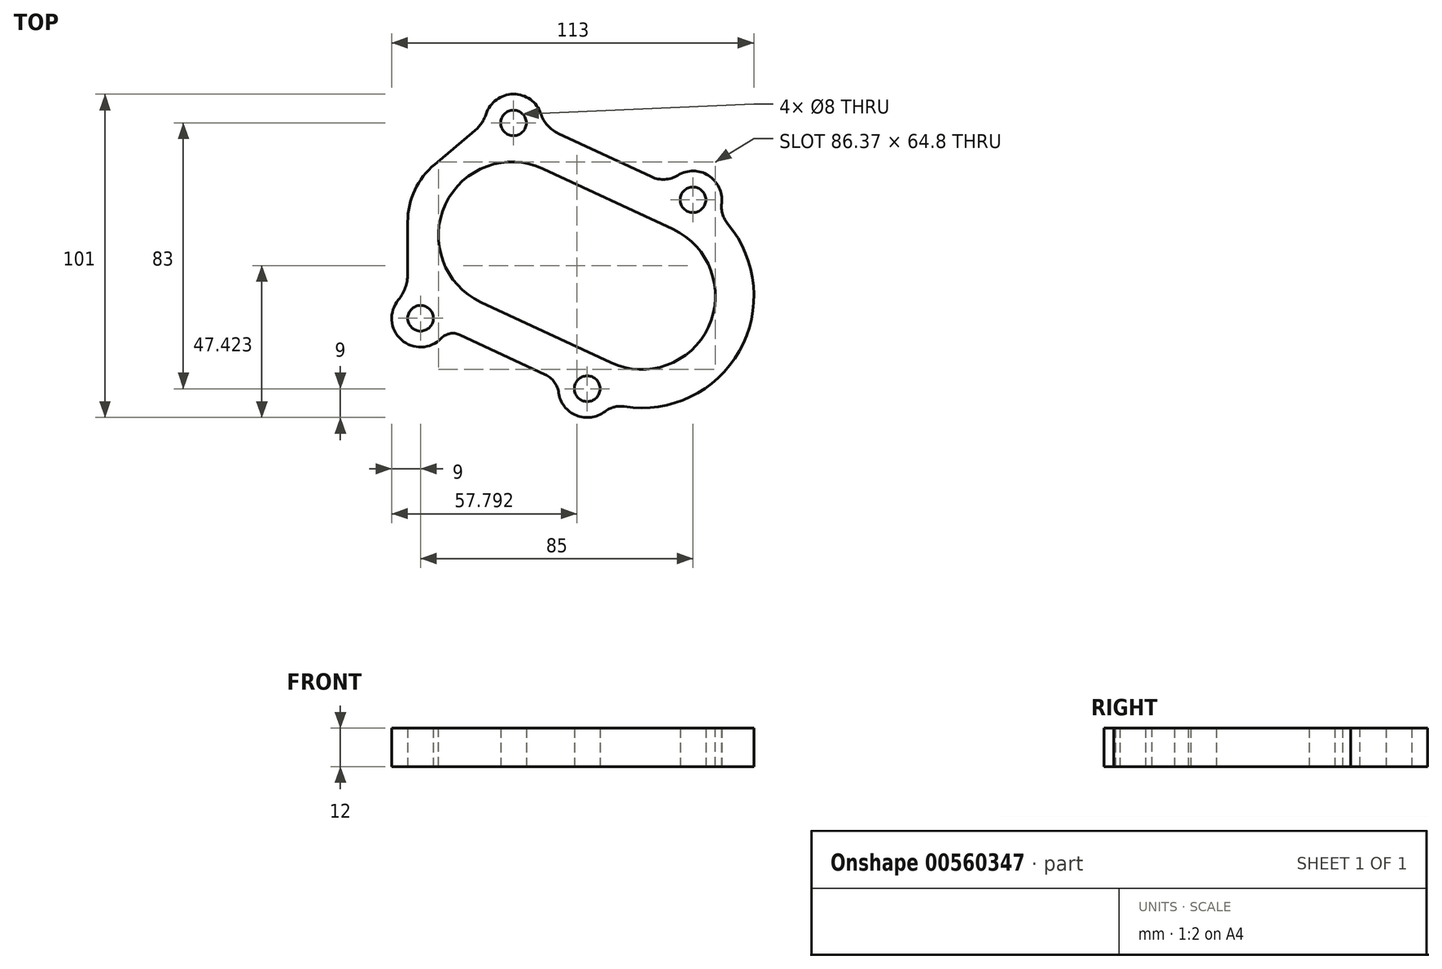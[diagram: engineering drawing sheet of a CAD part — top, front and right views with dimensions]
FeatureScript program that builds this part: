
annotation { "Feature Type Name" : "Feature", "Feature Type Description" : "" }
export const myFeature = defineFeature(function(context is Context, id is Id, definition is map)
    precondition{}
    {
        {
            var Q0;
            Q0=qCreatedBy(makeId("Top.planeOp"),FACE);
            var sketch = newSketch(context, id + "F0", { "sketchPlane" : qUnion([Q0])});
            skCircle(sketch, "E0", {"center": v(16, 30) * mm, "radius": 4 * mm});
            skCircle(sketch, "E1", {"center": v(-40, 54) * mm, "radius": 4 * mm});
            skLineSegment(sketch, "E2", {"start": v(-199.54, -60.76) * mm, "end": v(68.37, -60.76) * mm, "construction": true});
            skLineSegment(sketch, "E3", {"start": v(-129.38, -28.18) * mm, "end": v(-25.48, -76.62) * mm, "construction": true});
            skLineSegment(sketch, "E4", {"start": v(-199.68, -69.87) * mm, "end": v(-109.05, 6.17) * mm, "construction": true});
            skCircle(sketch, "E5", {"center": v(-17, -29) * mm, "radius": 4 * mm});
            skCircle(sketch, "E6", {"center": v(-69, -7) * mm, "radius": 4 * mm});
            skArc(sketch, "E7", {"start": v(-9.72, -20.85) * mm, "mid": v(20.85, -9.72) * mm, "end": v(9.72, 20.85) * mm});
            skLineSegment(sketch, "E8", {"start": v(-56.71, 32.04) * mm, "end": v(-43.51, 43.12) * mm});
            skLineSegment(sketch, "E9", {"start": v(9.72, 20.85) * mm, "end": v(-39.25, 43.68) * mm});
            skLineSegment(sketch, "E10", {"start": v(-9.72, -20.85) * mm, "end": v(-54.42, 0) * mm});
            skArc(sketch, "E11", {"start": v(-39.25, 43.68) * mm, "mid": v(-41.46, 44.02) * mm, "end": v(-43.51, 43.12) * mm});
            skLineSegment(sketch, "E12", {"start": v(-61, 22.85) * mm, "end": v(-61, 10.32) * mm});
            skArc(sketch, "E13", {"start": v(-56.71, 32.04) * mm, "mid": v(-59.88, 27.92) * mm, "end": v(-61, 22.85) * mm});
            skArc(sketch, "E14", {"start": v(-61, 10.32) * mm, "mid": v(-59.22, 4.2) * mm, "end": v(-54.42, 0) * mm});
            skArc(sketch, "E15", {"start": v(-31.47, 56.86) * mm, "mid": v(-40.02, 63) * mm, "end": v(-48.55, 56.82) * mm});
            skArc(sketch, "E16", {"start": v(-75.9, -1.23) * mm, "mid": v(-75, -13.7) * mm, "end": v(-62.5, -13.23) * mm});
            skArc(sketch, "E17", {"start": v(-25.91, -30.27) * mm, "mid": v(-20.4, -37.34) * mm, "end": v(-11.5, -36.13) * mm});
            skArc(sketch, "E18", {"start": v(11.27, 37.66) * mm, "mid": v(20.83, 37.6) * mm, "end": v(24.94, 28.96) * mm});
            skLineSegment(sketch, "E19", {"start": v(-26, 50.74) * mm, "end": v(3.08, 37.18) * mm});
            skLineSegment(sketch, "E20", {"start": v(-56.75, -12.16) * mm, "end": v(-30.14, -24.56) * mm});
            skLineSegment(sketch, "E21", {"start": v(-64.6, 41.1) * mm, "end": v(-52.1, 51.58) * mm});
            skLineSegment(sketch, "E22", {"start": v(-73, 23.07) * mm, "end": v(-73, 6.78) * mm});
            skArc(sketch, "E23", {"start": v(-64.6, 41.1) * mm, "mid": v(-70.8, 33.01) * mm, "end": v(-73, 23.07) * mm});
            skArc(sketch, "E24", {"start": v(-75.9, -1.23) * mm, "mid": v(-73.75, 2.52) * mm, "end": v(-73, 6.78) * mm});
            skArc(sketch, "E25", {"start": v(-56.75, -12.16) * mm, "mid": v(-59.8, -11.77) * mm, "end": v(-62.5, -13.23) * mm});
            skArc(sketch, "E26", {"start": v(-25.91, -30.27) * mm, "mid": v(-27.3, -26.88) * mm, "end": v(-30.14, -24.56) * mm});
            skArc(sketch, "E27", {"start": v(-52.1, 51.58) * mm, "mid": v(-49.96, 53.95) * mm, "end": v(-48.55, 56.82) * mm});
            skArc(sketch, "E28", {"start": v(-31.47, 56.86) * mm, "mid": v(-29.36, 53.24) * mm, "end": v(-26, 50.74) * mm});
            skArc(sketch, "E29", {"start": v(3.08, 37.18) * mm, "mid": v(7.24, 36.39) * mm, "end": v(11.27, 37.66) * mm});
            skArc(sketch, "E30", {"start": v(-5.43, -34.58) * mm, "mid": v(30.44, -17.27) * mm, "end": v(26.89, 22.4) * mm});
            skArc(sketch, "E31", {"start": v(24.94, 28.96) * mm, "mid": v(25.24, 25.48) * mm, "end": v(26.89, 22.4) * mm});
            skArc(sketch, "E32", {"start": v(-5.43, -34.58) * mm, "mid": v(-8.63, -34.73) * mm, "end": v(-11.5, -36.13) * mm});
            skSolve(sketch);
        }
        {
            var Q0;
            Q0=makeQuery(id+"F0.imprint","IMPRINT",FACE,{"disambiguationData":[TD([[makeQuery(id+"F0.imprint","IMPRINT",EDGE,{"derivedFrom":sQuery(id+"F0.wireOp",EDGE,"E7")}),1.0]])]});
            var Q1;
            Q1=makeQuery(id+"F0.imprint","IMPRINT",FACE,{"disambiguationData":[TD([[makeQuery(id+"F0.imprint","IMPRINT",EDGE,{"derivedFrom":sQuery(id+"F0.wireOp",EDGE,"E0")}),-1.0]])]});
            extrude(context, id + "F1", {"entities" : qUnion([Q0, Q1]), "depth" : 12 * mm, "offsetDistance" : 25 * mm});
        }
        {
            var Q0;
            Q0=qCreatedBy(makeId("Top.planeOp"),FACE);
            cPlane(context, id + "F2", {"entities" : qUnion([Q0]), "cplaneType" : CPlaneType.OFFSET, "offset" : 12 * mm, "width" : 150 * mm, "height" : 150 * mm});
        }
        {
            var Q0;
            Q0=qCreatedBy(id+"F2.planeOp",FACE);
            var sketch = newSketch(context, id + "F3", { "sketchPlane" : qUnion([Q0])});
            skCircle(sketch, "E33", {"center": v(0, 0) * mm, "radius": 23 * mm, "construction": true});
            skLineSegment(sketch, "E34", {"start": v(65.22, -34.61) * mm, "end": v(24.5, -34.61) * mm, "construction": true});
            skLineSegment(sketch, "E35", {"start": v(0, 0) * mm, "end": v(-78.97, 36.83) * mm, "construction": true});
            skCircle(sketch, "E36", {"center": v(-40.42, 18.85) * mm, "radius": 23 * mm, "construction": true});
            skArc(sketch, "E37", {"start": v(-30.7, 39.7) * mm, "mid": v(-61.26, 28.57) * mm, "end": v(-50.14, -2) * mm});
            skArc(sketch, "E38", {"start": v(-9.72, -20.85) * mm, "mid": v(20.85, -9.72) * mm, "end": v(9.72, 20.85) * mm});
            skLineSegment(sketch, "E39", {"start": v(-30.7, 39.7) * mm, "end": v(9.72, 20.85) * mm});
            skLineSegment(sketch, "E40", {"start": v(-50.14, -2) * mm, "end": v(-9.72, -20.85) * mm});
            skSolve(sketch);
        }
        {
            var Q0;
            Q0=sQuery(id+"F3.wireOp",EDGE,"E39");
            cPlane(context, id + "F4", {"entities" : qUnion([Q0]), "cplaneType" : CPlaneType.LINE_ANGLE, "offset" : 25 * mm, "angle" : 0 * degree, "width" : 150 * mm, "height" : 150 * mm});
        }
        {
            var Q0;
            Q0=makeQuery(id+"F3.imprint","IMPRINT",FACE,{"disambiguationData":[TD([[makeQuery(id+"F3.imprint","IMPRINT",EDGE,{"derivedFrom":sQuery(id+"F3.wireOp",EDGE,"E37")}),1.0]])]});
            extrude(context, id + "F5", {"entities" : qUnion([Q0]), "operationType" : NewBodyOperationType.REMOVE, "oppositeDirection" : true, "depth" : 25 * mm, "offsetDistance" : 25 * mm});
        }
    });
